# Revit family: Hager-Orion-IP66-D500-Cl.I-Inox_encl-630A-CH-fr
name_source: partatom
category: Equipement électrique
units: mm (PartAtom-declared; Revit-internal decimal feet)

## family parameters
Configuration du panneau = Deux colonnes, circuits au sein
Cote de connecteur circulaire = Utiliser le diamètre
Couper avec des vides une fois chargée = Non
Hôte = Face
Partagée = Non
Point de calcul de pièce = Non
Type d'élément = Tableau de raccordement

## types (2) — shared parameters
EF001088 - possibilité de montage en saillie = Oui
EF003532 - convient pour utilisation à l’extérieur = Oui
EF006244 - couvercle/porte transparent(e) = Non
EF009170 - épaisseur de matériau du boîtier = 2 mm  [stored 0.00656168 ft]
EF009171 - épaisseur de matériau de la porte/du couvercle = 2 mm  [stored 0.00656168 ft]
Fabricant = Hager
HG000002 - avec porte = Oui
HG000024 - Hauteur de la section basse = 800 mm  [stored 2.62467 ft]
zero-valued in all types: EF000437 - nombre d'entrées de conduit, EF002950 - largeur en nombre de modules, EF004427 - nombre de modules, EF009554 - nombre d'ouvertures pour plaques à bride, Elévation par défaut, HG000027 - Hauteur du socle

## per-type parameters (varying)
- saillie IP55 L1200 H1400 P300  - FL064BWL: EF000008 - largeur=350 mm  [stored 1.14829 ft]; EF000040 - hauteur=300 mm; EF000049 - profondeur=160 mm  [stored 0.524934 ft]; EF000118 - avec cadre/support de montage=Oui; EF000218 - profondeur d'encastrement=200 mm  [stored 0.656168 ft]; EF000266 - nombre de rangées=2; EF001131 - profondeur intérieure=400 mm  [stored 1.31234 ft]; EF006306 - avec serrure=Oui; EF007800 - adapté à un parafoudre=Oui; EF008873 - courant nominal (In)=0 A; EF015940 - couvercle avec décharge de pression=Oui; HG000006 - Encastré=Oui; HG000009 - Porte à double battant=Non; HG000010 - Portes asymétriques=Non; HG000023 - Armoire double section=Oui; HG000026 - Installation au sol=Oui
- saillie IP66 L800 H1000 P300  - FL042BWL: Commentaires du type=Orion; EF000003 - mode de pose=EV000384 - saillie; EF000007 - couleur=EV000154 - autre; EF000008 - largeur=800 mm  [stored 2.62467 ft]; EF000040 - hauteur=1000 mm  [stored 3.28084 ft]; EF000049 - profondeur=300 mm; EF000118 - avec cadre/support de montage=Non; EF000218 - profondeur d'encastrement=0 mm  [stored 0 ft]; EF000266 - nombre de rangées=0; EF000339 - type de capot=EV004216 - porte; EF001131 - profondeur intérieure=266 mm; EF001596 - matériau du boîtier/corps=EV000166 - acier inoxydable; EF004293 - indice de protection contre les chocs (IK)=EV008784 - IK10; EF004464 - type de porte=EV002646 - unique; EF005474 - indice de protection (IP)=EV006422 - IP66; EF006306 - avec serrure=Non; EF007800 - adapté à un parafoudre=Non; EF008873 - courant nominal (In)=630 A; EF009212 - finition du couvercle=EV009916 - avec échancrure; EF015940 - couvercle avec décharge de pression=Non; HG000003 - Gamme=Orion; HG000004 - Référence fabricant=FL042BWL; HG000006 - Encastré=Non; HG000009 - Porte à double battant=Oui; HG000010 - Portes asymétriques=Oui; HG000023 - Armoire double section=Non; HG000026 - Installation au sol=Non

note: [stored X ft] marks values corroborated as IEEE doubles in the binary element streams (Revit-internal decimal feet)

## geometry (parser evidence)
native form markers: Sweep x6
no freeform markers — native parametric forms only
